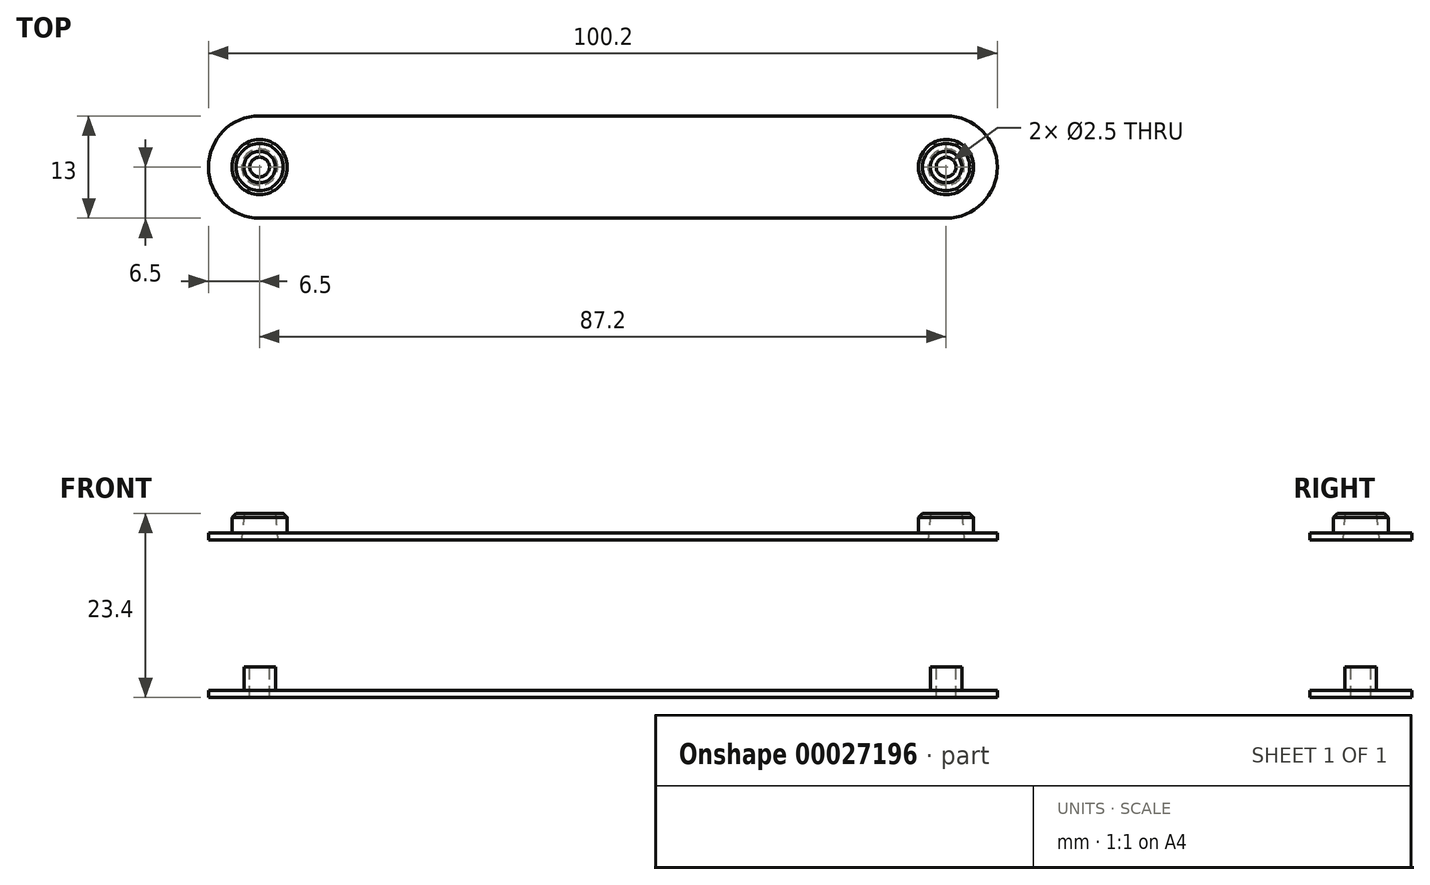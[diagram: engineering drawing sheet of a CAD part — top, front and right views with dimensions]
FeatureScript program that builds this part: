
annotation { "Feature Type Name" : "Feature", "Feature Type Description" : "" }
export const myFeature = defineFeature(function(context is Context, id is Id, definition is map)
    precondition{}
    {
        {
            var Q0;
            Q0=qCreatedBy(makeId("Top.planeOp"),FACE);
            var sketch = newSketch(context, id + "F0", { "sketchPlane" : qUnion([Q0])});
            skLineSegment(sketch, "E0", {"start": v(0, 0) * mm, "end": v(-87.2, 0) * mm, "construction": true});
            skCircle(sketch, "E1", {"center": v(-87.2, 0) * mm, "radius": 3.5 * mm});
            skCircle(sketch, "E2", {"center": v(0, 0) * mm, "radius": 3.5 * mm});
            skCircle(sketch, "E3.0", {"center": v(-87.2, 0) * mm, "radius": 6.5 * mm});
            skCircle(sketch, "E4.0", {"center": v(0, 0) * mm, "radius": 6.5 * mm});
            skLineSegment(sketch, "E5", {"start": v(0, -6.5) * mm, "end": v(-87.2, -6.5) * mm});
            skLineSegment(sketch, "E6", {"start": v(-87.25, 6.5) * mm, "end": v(0, 6.5) * mm});
            skSolve(sketch);
        }
        {
            var Q0;
            Q0=makeQuery(id+"F0.imprint","IMPRINT",FACE,{"disambiguationData":[TD([[makeQuery(id+"F0.imprint","IMPRINT",EDGE,{"derivedFrom":sQuery(id+"F0.wireOp",EDGE,"E1")}),1.0]])]});
            var Q1;
            Q1=makeQuery(id+"F0.imprint","IMPRINT",FACE,{"disambiguationData":[TD([[makeQuery(id+"F0.imprint","IMPRINT",EDGE,{"derivedFrom":sQuery(id+"F0.wireOp",EDGE,"E1")}),-1.0]])]});
            var Q2;
            {var subQ5=sQuery(id+"F0.wireOp",EDGE,"E5");Q2=makeQuery(id+"F0.imprint","IMPRINT",FACE,{"disambiguationData":[TD([[makeQuery(id+"F0.imprint","IMPRINT",EDGE,{"derivedFrom":subQ5}),-1.0]])]});}
            var Q3;
            Q3=makeQuery(id+"F0.imprint","IMPRINT",FACE,{"disambiguationData":[TD([[makeQuery(id+"F0.imprint","IMPRINT",EDGE,{"derivedFrom":sQuery(id+"F0.wireOp",EDGE,"E2")}),-1.0]])]});
            var Q4;
            Q4=makeQuery(id+"F0.imprint","IMPRINT",FACE,{"disambiguationData":[TD([[makeQuery(id+"F0.imprint","IMPRINT",EDGE,{"derivedFrom":sQuery(id+"F0.wireOp",EDGE,"E2")}),1.0]])]});
            extrude(context, id + "F1", {"entities" : qUnion([Q0, Q1, Q2, Q3, Q4]), "oppositeDirection" : true, "depth" : 0.9 * mm});
        }
        {
            var Q0;
            Q0=makeQuery(id+"F0.imprint","IMPRINT",FACE,{"disambiguationData":[TD([[makeQuery(id+"F0.imprint","IMPRINT",EDGE,{"derivedFrom":sQuery(id+"F0.wireOp",EDGE,"E1")}),1.0]])]});
            var Q1;
            Q1=makeQuery(id+"F0.imprint","IMPRINT",FACE,{"disambiguationData":[TD([[makeQuery(id+"F0.imprint","IMPRINT",EDGE,{"derivedFrom":sQuery(id+"F0.wireOp",EDGE,"E2")}),1.0]])]});
            var Q2;
            Q2=sQuery(id+"F0.wireOp",EDGE,"E1");
            var Q3;
            Q3=sQuery(id+"F0.wireOp",EDGE,"E2");
            extrude(context, id + "F2", {"entities" : qUnion([Q0, Q1]), "operationType" : NewBodyOperationType.ADD, "surfaceEntities" : qUnion([Q2, Q3]), "depth" : 2.5 * mm});
        }
        {
            var Q0;
            Q0=makeQuery(id+"F2.opExtrude","CAP_FACE",FACE,{"disambiguationData":[OSD([sQuery(id+"F0.wireOp",EDGE,"E1")])],"isStart":false});
            var sketch = newSketch(context, id + "F3", { "sketchPlane" : qUnion([Q0])});
            skCircle(sketch, "E7", {"center": v(-87.2, 0) * mm, "radius": 2 * mm});
            skSolve(sketch);
        }
        {
            var Q0;
            Q0=makeQuery(id+"F2.opExtrude","CAP_FACE",FACE,{"disambiguationData":[OSD([sQuery(id+"F0.wireOp",EDGE,"E2")])],"isStart":false});
            var sketch = newSketch(context, id + "F4", { "sketchPlane" : qUnion([Q0])});
            skCircle(sketch, "E8", {"center": v(0, 0) * mm, "radius": 2 * mm});
            skSolve(sketch);
        }
        {
            var Q0;
            Q0=makeQuery(id+"F3.imprint","IMPRINT",FACE,{"disambiguationData":[TD([[makeQuery(id+"F3.imprint","IMPRINT",EDGE,{"derivedFrom":sQuery(id+"F3.wireOp",EDGE,"E7")}),1.0]])]});
            var Q1;
            Q1=makeQuery(id+"F4.imprint","IMPRINT",FACE,{"disambiguationData":[TD([[makeQuery(id+"F4.imprint","IMPRINT",EDGE,{"derivedFrom":sQuery(id+"F4.wireOp",EDGE,"E8")}),1.0]])]});
            var Q2;
            Q2=sQuery(id+"F3.wireOp",EDGE,"E7");
            var Q3;
            Q3=sQuery(id+"F4.wireOp",EDGE,"E8");
            extrude(context, id + "F5", {"entities" : qUnion([Q0, Q1]), "operationType" : NewBodyOperationType.REMOVE, "surfaceEntities" : qUnion([Q2, Q3]), "endBound" : BoundingType.THROUGH_ALL, "oppositeDirection" : true, "depth" : 25 * mm, "hasDraft" : true, "draftAngle" : 5 * degree});
        }
        {
            var Q0;
            Q0=makeQuery(id+"F2.opExtrude","CAP_EDGE",EDGE,{"disambiguationData":[OSD([sQuery(id+"F0.wireOp",EDGE,"E1")])],"isStart":false});
            var Q1;
            Q1=makeQuery(id+"F2.opExtrude","CAP_EDGE",EDGE,{"disambiguationData":[OSD([sQuery(id+"F0.wireOp",EDGE,"E2")])],"isStart":false});
            chamfer(context, id + "F6", {"entities" : qUnion([Q0, Q1]), "width" : 0.5 * mm, "tangentPropagation" : true});
        }
        {
            var Q0;
            Q0=qCreatedBy(makeId("Top.planeOp"),FACE);
            cPlane(context, id + "F7", {"entities" : qUnion([Q0]), "cplaneType" : CPlaneType.OFFSET, "offset" : 20 * mm, "oppositeDirection" : true, "width" : 150 * mm, "height" : 150 * mm});
        }
        {
            var Q0;
            Q0=qCreatedBy(id+"F7.planeOp",FACE);
            var sketch = newSketch(context, id + "F8", { "sketchPlane" : qUnion([Q0])});
            skCircle(sketch, "E9.0", {"center": v(0, 0) * mm, "radius": 2 * mm});
            skCircle(sketch, "E10.0", {"center": v(-87.2, 0) * mm, "radius": 2 * mm});
            skLineSegment(sketch, "E11.0", {"start": v(0, -6.5) * mm, "end": v(-87.2, -6.5) * mm});
            skArc(sketch, "E12.0", {"start": v(-87.25, 6.5) * mm, "mid": v(-93.7, -0.03) * mm, "end": v(-87.2, -6.5) * mm});
            skLineSegment(sketch, "E13.0", {"start": v(-87.25, 6.5) * mm, "end": v(0, 6.5) * mm});
            skArc(sketch, "E14.0", {"start": v(0, -6.5) * mm, "mid": v(6.5, 0) * mm, "end": v(0, 6.5) * mm});
            skSolve(sketch);
        }
        {
            var Q0;
            Q0=makeQuery(id+"F8.imprint","IMPRINT",FACE,{"disambiguationData":[TD([[makeQuery(id+"F8.imprint","IMPRINT",EDGE,{"derivedFrom":sQuery(id+"F8.wireOp",EDGE,"E9.0")}),-1.0]])]});
            var Q1;
            Q1=makeQuery(id+"F8.imprint","IMPRINT",FACE,{"disambiguationData":[TD([[makeQuery(id+"F8.imprint","IMPRINT",EDGE,{"derivedFrom":sQuery(id+"F8.wireOp",EDGE,"E9.0")}),1.0]])]});
            var Q2;
            Q2=makeQuery(id+"F8.imprint","IMPRINT",FACE,{"disambiguationData":[TD([[makeQuery(id+"F8.imprint","IMPRINT",EDGE,{"derivedFrom":sQuery(id+"F8.wireOp",EDGE,"E10.0")}),1.0]])]});
            extrude(context, id + "F9", {"entities" : qUnion([Q0, Q1, Q2]), "oppositeDirection" : true, "depth" : 0.9 * mm});
        }
        {
            var Q0;
            Q0=makeQuery(id+"F8.imprint","IMPRINT",FACE,{"disambiguationData":[TD([[makeQuery(id+"F8.imprint","IMPRINT",EDGE,{"derivedFrom":sQuery(id+"F8.wireOp",EDGE,"E10.0")}),1.0]])]});
            var Q1;
            Q1=makeQuery(id+"F8.imprint","IMPRINT",FACE,{"disambiguationData":[TD([[makeQuery(id+"F8.imprint","IMPRINT",EDGE,{"derivedFrom":sQuery(id+"F8.wireOp",EDGE,"E9.0")}),1.0]])]});
            extrude(context, id + "F10", {"entities" : qUnion([Q0, Q1]), "operationType" : NewBodyOperationType.ADD, "depth" : 3 * mm});
        }
        {
            var Q0;
            Q0=makeQuery(id+"F10.opExtrude","CAP_FACE",FACE,{"disambiguationData":[OSD([sQuery(id+"F8.wireOp",EDGE,"E10.0")])],"isStart":false});
            var sketch = newSketch(context, id + "F11", { "sketchPlane" : qUnion([Q0])});
            skCircle(sketch, "E15", {"center": v(-87.2, 0) * mm, "radius": 1.25 * mm});
            skSolve(sketch);
        }
        {
            var Q0;
            Q0=makeQuery(id+"F10.opExtrude","CAP_FACE",FACE,{"disambiguationData":[OSD([sQuery(id+"F8.wireOp",EDGE,"E9.0")])],"isStart":false});
            var sketch = newSketch(context, id + "F12", { "sketchPlane" : qUnion([Q0])});
            skCircle(sketch, "E16", {"center": v(0, 0) * mm, "radius": 1.25 * mm});
            skSolve(sketch);
        }
        {
            var Q0;
            Q0=makeQuery(id+"F11.imprint","IMPRINT",FACE,{"disambiguationData":[TD([[makeQuery(id+"F11.imprint","IMPRINT",EDGE,{"derivedFrom":sQuery(id+"F11.wireOp",EDGE,"E15")}),1.0]])]});
            var Q1;
            Q1=makeQuery(id+"F12.imprint","IMPRINT",FACE,{"disambiguationData":[TD([[makeQuery(id+"F12.imprint","IMPRINT",EDGE,{"derivedFrom":sQuery(id+"F12.wireOp",EDGE,"E16")}),1.0]])]});
            extrude(context, id + "F13", {"entities" : qUnion([Q0, Q1]), "operationType" : NewBodyOperationType.REMOVE, "endBound" : BoundingType.THROUGH_ALL, "oppositeDirection" : true, "depth" : 25 * mm});
        }
    });
